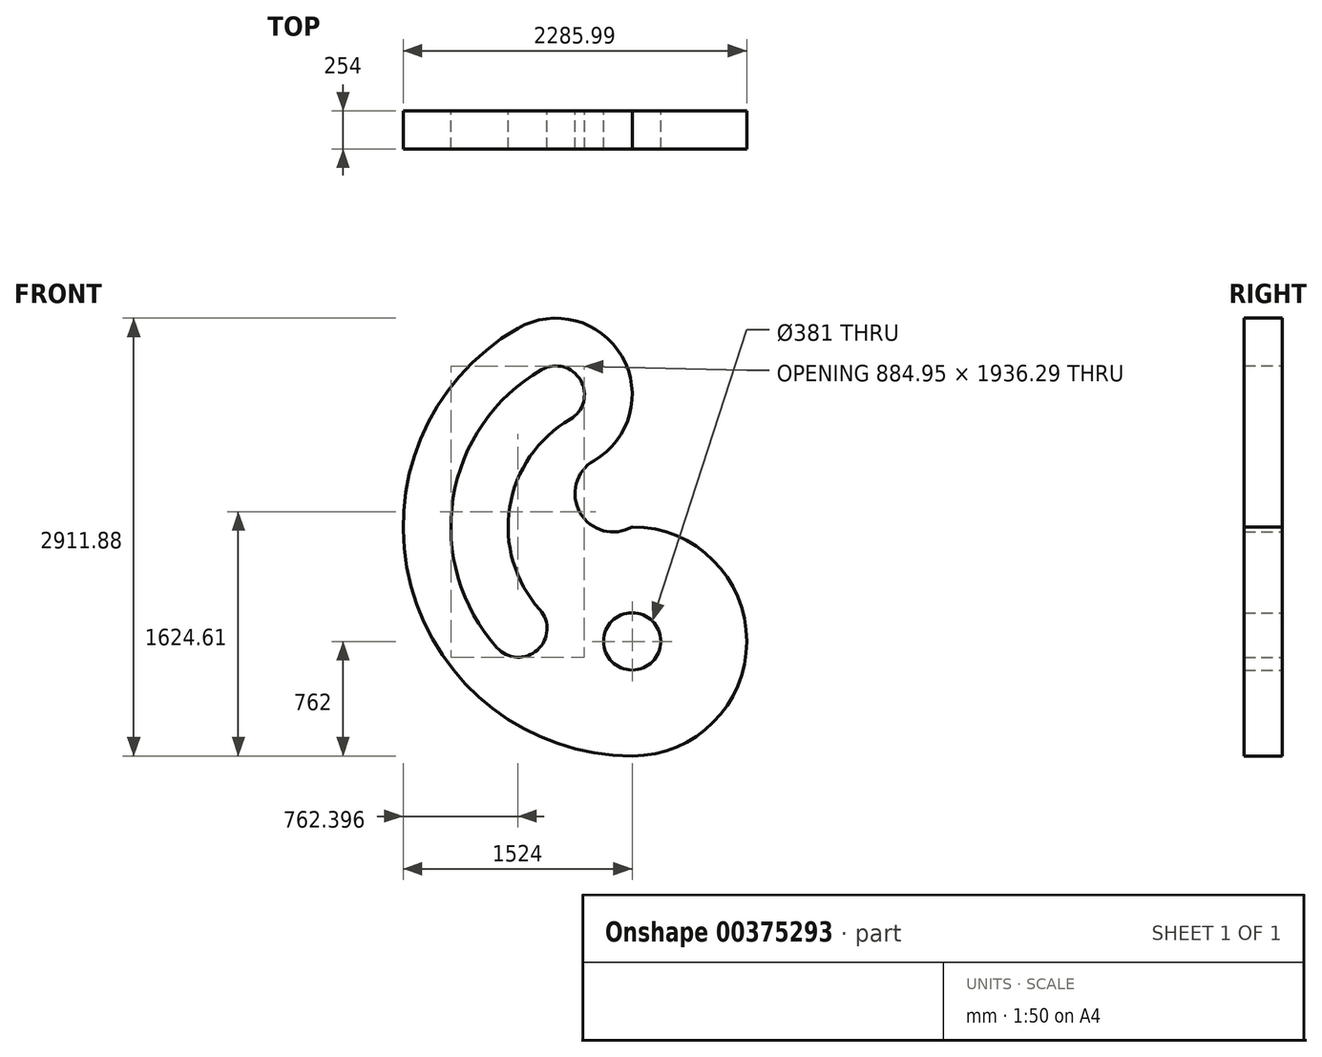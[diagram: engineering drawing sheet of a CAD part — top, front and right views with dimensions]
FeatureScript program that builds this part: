
annotation { "Feature Type Name" : "Feature", "Feature Type Description" : "" }
export const myFeature = defineFeature(function(context is Context, id is Id, definition is map)
    precondition{}
    {
        {
            var Q0;
            Q0=qCreatedBy(makeId("Front.planeOp"),FACE);
            var sketch = newSketch(context, id + "F0", { "sketchPlane" : qUnion([Q0])});
            skCircle(sketch, "E0", {"center": v(0, 0) * mm, "radius": 190.5 * mm});
            skArc(sketch, "E1", {"start": v(-762, 2081.82) * mm, "mid": v(-1472.07, 367.56) * mm, "end": v(0, -762) * mm});
            skArc(sketch, "E2", {"start": v(-254, 1201.94) * mm, "mid": v(-68.06, 1895.88) * mm, "end": v(-762, 2081.82) * mm});
            skArc(sketch, "E3", {"start": v(-254, 1201.94) * mm, "mid": v(-346.97, 854.97) * mm, "end": v(0, 762) * mm});
            skArc(sketch, "E4", {"start": v(-412.75, 1476.9) * mm, "mid": v(-343.02, 1737.13) * mm, "end": v(-603.25, 1806.86) * mm});
            skArc(sketch, "E5", {"start": v(-899.27, -42.33) * mm, "mid": v(-630.28, -57.32) * mm, "end": v(-615.3, 211.67) * mm});
            skArc(sketch, "E6.trimOffspring", {"start": v(0, -762) * mm, "mid": v(761.99, 0) * mm, "end": v(0, 762) * mm});
            skArc(sketch, "E7.0", {"start": v(-412.75, 1476.9) * mm, "mid": v(-815.12, 892.49) * mm, "end": v(-615.3, 211.67) * mm});
            skArc(sketch, "E8.0", {"start": v(-603.25, 1806.86) * mm, "mid": v(-1191.33, 952.71) * mm, "end": v(-899.27, -42.33) * mm});
            skSolve(sketch);
        }
        {
            var Q0;
            Q0=makeQuery(id+"F0.imprint","IMPRINT",FACE,{"disambiguationData":[TD([[makeQuery(id+"F0.imprint","IMPRINT",EDGE,{"derivedFrom":sQuery(id+"F0.wireOp",EDGE,"E0")}),-1.0]])]});
            extrude(context, id + "F1", {"entities" : qUnion([Q0]), "depth" : 254 * mm});
        }
    });
